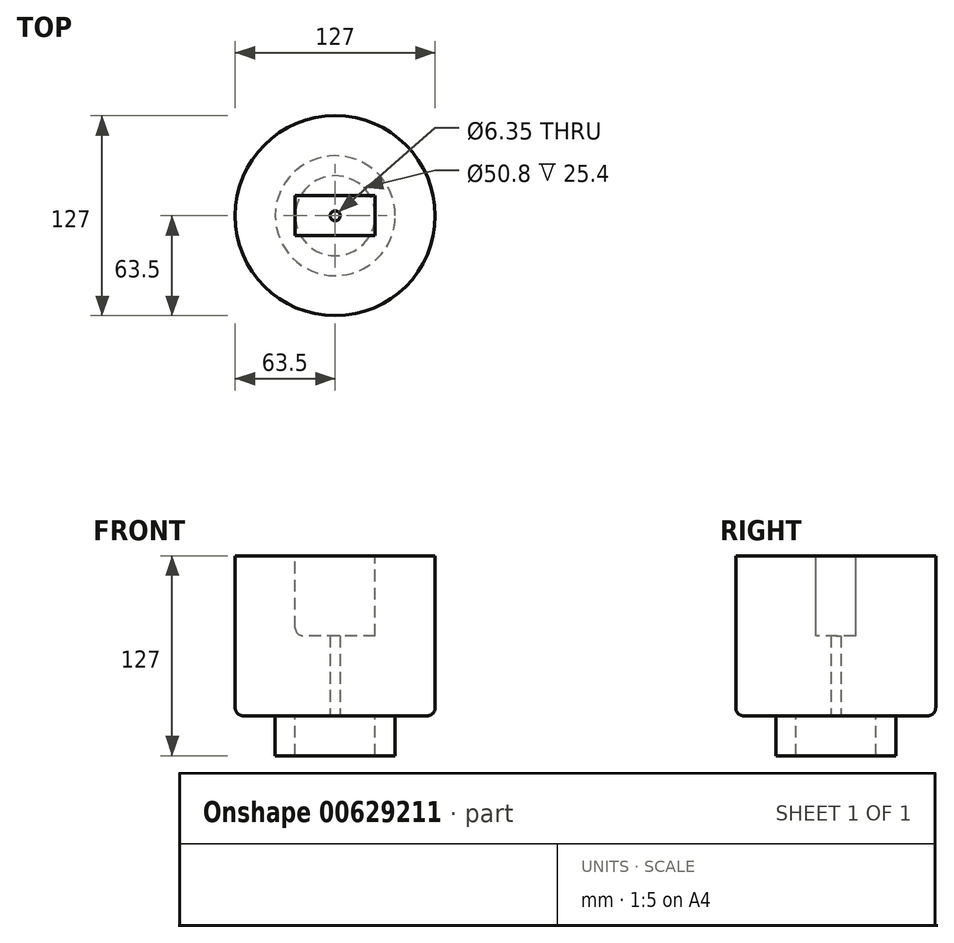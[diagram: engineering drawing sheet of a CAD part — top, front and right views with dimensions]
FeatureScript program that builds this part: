
annotation { "Feature Type Name" : "Feature", "Feature Type Description" : "" }
export const myFeature = defineFeature(function(context is Context, id is Id, definition is map)
    precondition{}
    {
        {
            var Q0;
            Q0=qCreatedBy(makeId("Top.planeOp"),FACE);
            var sketch = newSketch(context, id + "F0", { "sketchPlane" : qUnion([Q0])});
            skCircle(sketch, "E0", {"center": v(0, 0) * mm, "radius": 63.5 * mm});
            skSolve(sketch);
        }
        {
            var Q0;
            Q0=makeQuery(id+"F0.imprint","IMPRINT",FACE,{"disambiguationData":[TD([[makeQuery(id+"F0.imprint","IMPRINT",EDGE,{"derivedFrom":sQuery(id+"F0.wireOp",EDGE,"E0")}),1.0]])]});
            extrude(context, id + "F1", {"entities" : qUnion([Q0]), "endBound" : BoundingType.SYMMETRIC, "depth" : 101.6 * mm, "offsetDistance" : 25.4 * mm});
        }
        {
            var Q0;
            Q0=makeQuery(id+"F1.opExtrude","CAP_FACE",FACE,{"disambiguationData":[OSD([sQuery(id+"F0.wireOp",EDGE,"E0")])],"isStart":false});
            var sketch = newSketch(context, id + "F2", { "sketchPlane" : qUnion([Q0])});
            skLineSegment(sketch, "E1.bottom", {"start": v(25.4, 12.7) * mm, "end": v(-25.4, 12.7) * mm});
            skLineSegment(sketch, "E1.top", {"start": v(25.4, -12.7) * mm, "end": v(-25.4, -12.7) * mm});
            skLineSegment(sketch, "E1.left", {"start": v(25.4, 12.7) * mm, "end": v(25.4, -12.7) * mm});
            skLineSegment(sketch, "E1.right", {"start": v(-25.4, 12.7) * mm, "end": v(-25.4, -12.7) * mm});
            skPoint(sketch, "E1.middle", {"position": v(0, 0) * mm});
            skSolve(sketch);
        }
        {
            var Q0;
            Q0=makeQuery(id+"F2.imprint","IMPRINT",FACE,{"disambiguationData":[TD([[makeQuery(id+"F2.imprint","IMPRINT",EDGE,{"derivedFrom":sQuery(id+"F2.wireOp",EDGE,"E1.bottom")}),1.0]])]});
            extrude(context, id + "F3", {"entities" : qUnion([Q0]), "operationType" : NewBodyOperationType.REMOVE, "oppositeDirection" : true, "depth" : 50.8 * mm, "offsetDistance" : 25.4 * mm});
        }
        {
            var Q0;
            Q0=makeQuery(id+"F1.opExtrude","CAP_FACE",FACE,{"disambiguationData":[OSD([sQuery(id+"F0.wireOp",EDGE,"E0")])],"isStart":true});
            var sketch = newSketch(context, id + "F4", { "sketchPlane" : qUnion([Q0])});
            skPoint(sketch, "E2", {"position": v(0, 0) * mm});
            skSolve(sketch);
        }
        {
            var Q0;
            Q0=sQuery(id+"F4.wireOp",VERTEX,"E2");
            var Q1;
            Q1=makeQuery(id+"F1.opExtrude","SWEPT_BODY",BODY,{"disambiguationData":[OSD([sQuery(id+"F0.wireOp",EDGE,"E0")])]});
            hole(context, id + "F5", {"style" : HoleStyle.SIMPLE, "endStyle" : HoleEndStyle.THROUGH, "holeDiameter" : 6.35 * mm, "majorDiameter" : 6.35 * mm, "isTappedThrough" : true, "tappedDepth" : 12.7 * mm, "tapClearance" : 3, "locations" : qUnion([Q0]), "scope" : qUnion([Q1])});
        }
        {
            var Q0;
            Q0=makeQuery(id+"F1.opExtrude","CAP_EDGE",EDGE,{"disambiguationData":[OSD([sQuery(id+"F0.wireOp",EDGE,"E0")])],"isStart":true});
            fillet(context, id + "F6", {"entities" : qUnion([Q0]), "radius" : 5.08 * mm, "tangentPropagation" : true, "allowEdgeOverflow" : false});
        }
        {
            var Q0;
            Q0=makeQuery(id+"F3.boolean.opBoolean","COPY",EDGE,{"derivedFrom":makeQuery(id+"F3.opExtrude","CAP_EDGE",EDGE,{"disambiguationData":[OSD([sQuery(id+"F2.wireOp",EDGE,"E1.right")])],"isStart":false})});
            fillet(context, id + "F7", {"entities" : qUnion([Q0]), "radius" : 5.08 * mm, "tangentPropagation" : true, "allowEdgeOverflow" : false});
        }
        {
            var Q0;
            Q0=qCreatedBy(makeId("Front.planeOp"),FACE);
            var sketch = newSketch(context, id + "F8", { "sketchPlane" : qUnion([Q0])});
            skLineSegment(sketch, "E3.bottom", {"start": v(-38.1, -50.8) * mm, "end": v(-25.4, -50.8) * mm});
            skLineSegment(sketch, "E3.top", {"start": v(-38.1, -76.2) * mm, "end": v(-25.4, -76.2) * mm});
            skLineSegment(sketch, "E3.left", {"start": v(-38.1, -50.8) * mm, "end": v(-38.1, -76.2) * mm});
            skLineSegment(sketch, "E3.right", {"start": v(-25.4, -50.8) * mm, "end": v(-25.4, -76.2) * mm});
            skLineSegment(sketch, "E4", {"start": v(0, 58.26) * mm, "end": v(0, -19.47) * mm});
            skSolve(sketch);
        }
        {
            var Q0;
            Q0=makeQuery(id+"F8.imprint","IMPRINT",FACE,{"disambiguationData":[TD([[makeQuery(id+"F8.imprint","IMPRINT",EDGE,{"derivedFrom":sQuery(id+"F8.wireOp",EDGE,"E3.bottom")}),-1.0]])]});
            var Q1;
            Q1=sQuery(id+"F8.wireOp",EDGE,"E4");
            revolve(context, id + "F9", {"operationType" : NewBodyOperationType.ADD, "entities" : qUnion([Q0]), "axis" : qUnion([Q1]), "revolveType" : RevolveType.FULL});
        }
    });
